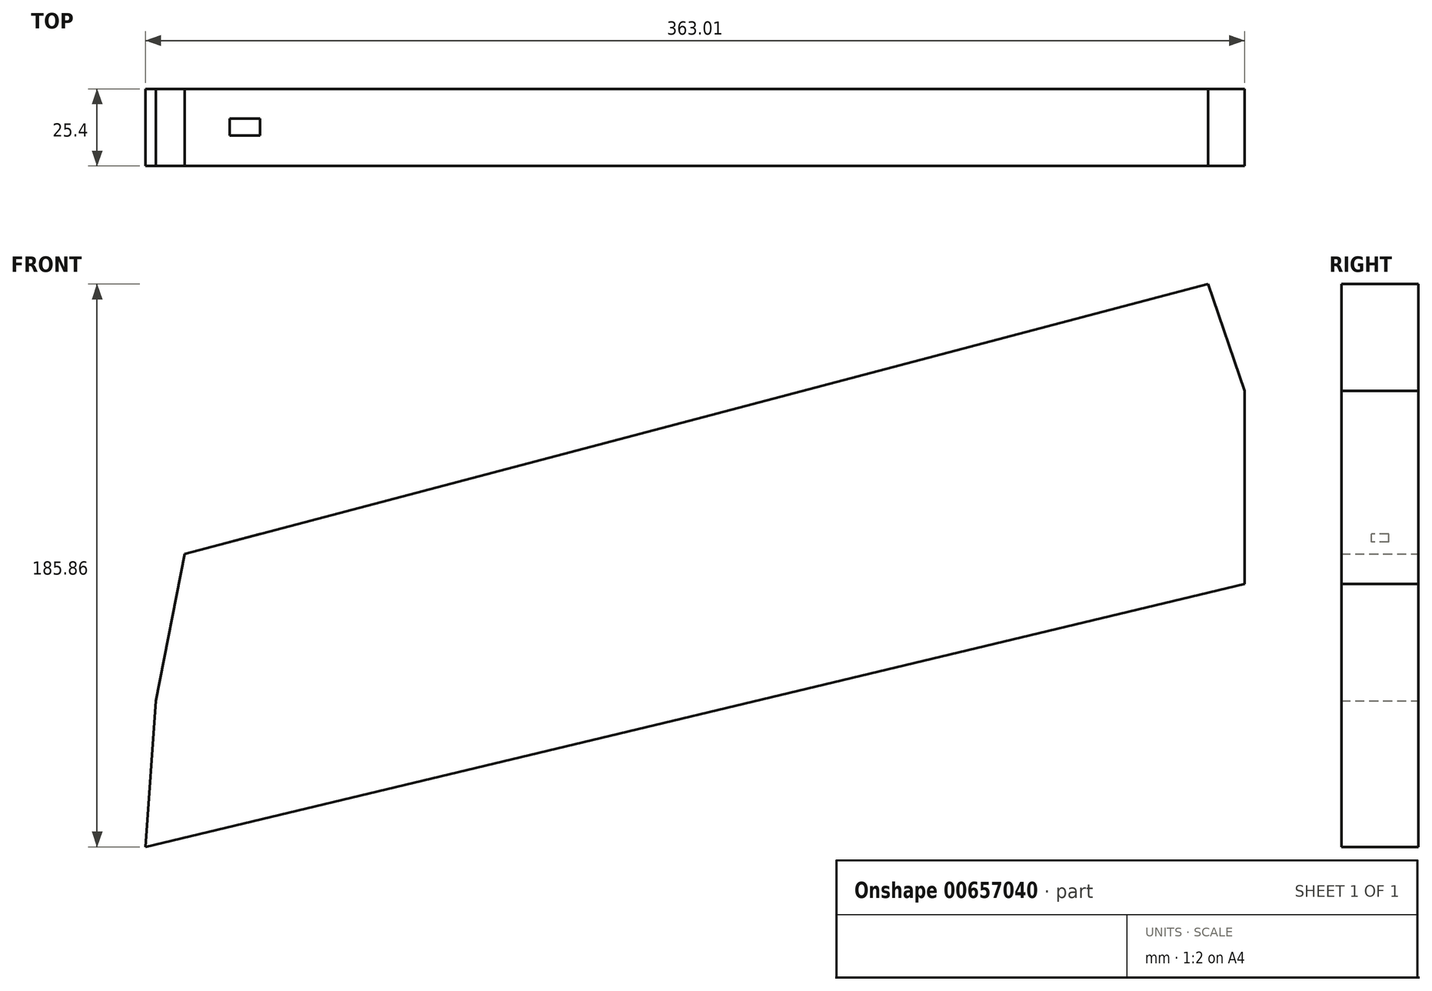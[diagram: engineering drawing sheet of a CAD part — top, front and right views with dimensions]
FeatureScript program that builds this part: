
annotation { "Feature Type Name" : "Feature", "Feature Type Description" : "" }
export const myFeature = defineFeature(function(context is Context, id is Id, definition is map)
    precondition{}
    {
        {
            var Q0;
            Q0=qCreatedBy(makeId("Front.planeOp"),FACE);
            var sketch = newSketch(context, id + "F0", { "sketchPlane" : qUnion([Q0])});
            skLineSegment(sketch, "E0", {"start": v(-183.67, -33.37) * mm, "end": v(179.34, 53.4) * mm});
            skLineSegment(sketch, "E1", {"start": v(179.34, 53.4) * mm, "end": v(179.34, 117.14) * mm});
            skLineSegment(sketch, "E2", {"start": v(179.34, 117.14) * mm, "end": v(131.4, 143.01) * mm});
            skLineSegment(sketch, "E3", {"start": v(131.4, 143.01) * mm, "end": v(-170.69, 63.38) * mm});
            skLineSegment(sketch, "E4", {"start": v(-170.69, 63.38) * mm, "end": v(-129.23, 55.16) * mm});
            skLineSegment(sketch, "E5", {"start": v(-129.23, 55.16) * mm, "end": v(-170.69, 63.38) * mm});
            skLineSegment(sketch, "E6", {"start": v(-170.69, 63.38) * mm, "end": v(-180.32, 14.8) * mm});
            skLineSegment(sketch, "E7", {"start": v(-180.32, 14.8) * mm, "end": v(-183.67, -33.37) * mm});
            skLineSegment(sketch, "E8", {"start": v(-170.69, 63.38) * mm, "end": v(-135.73, 72.6) * mm});
            skLineSegment(sketch, "E9", {"start": v(131.4, 143.01) * mm, "end": v(167.35, 152.49) * mm});
            skLineSegment(sketch, "E10", {"start": v(167.35, 152.49) * mm, "end": v(179.34, 117.14) * mm});
            skSolve(sketch);
        }
        {
            var Q0;
            Q0 = qSketchRegion(id + "F0", true);
            extrude(context, id + "F1", {"entities" : qUnion([Q0]), "depth" : 25.4 * mm, "offsetDistance" : 25.4 * mm});
        }
        {
            var Q0;
            Q0=makeQuery(id+"F1.opExtrude","SWEPT_FACE",FACE,{"disambiguationData":[OSD([sQuery(id+"F0.wireOp",EDGE,"E3"),sQuery(id+"F0.wireOp",EDGE,"E8"),sQuery(id+"F0.wireOp",EDGE,"E9")])]});
            var sketch = newSketch(context, id + "F2", { "sketchPlane" : qUnion([Q0])});
            skLineSegment(sketch, "E11.bottom", {"start": v(-133.6, -9.76) * mm, "end": v(-123.24, -9.76) * mm});
            skLineSegment(sketch, "E11.top", {"start": v(-133.6, -15.4) * mm, "end": v(-123.24, -15.4) * mm});
            skLineSegment(sketch, "E11.left", {"start": v(-133.6, -9.76) * mm, "end": v(-133.6, -15.4) * mm});
            skLineSegment(sketch, "E11.right", {"start": v(-123.24, -9.76) * mm, "end": v(-123.24, -15.4) * mm});
            skSolve(sketch);
        }
        {
            var Q0;
            Q0 = qSketchRegion(id + "F2", true);
            extrude(context, id + "F3", {"entities" : qUnion([Q0]), "operationType" : NewBodyOperationType.ADD, "depth" : 0.03 * mm, "offsetDistance" : 25.4 * mm});
        }
    });
